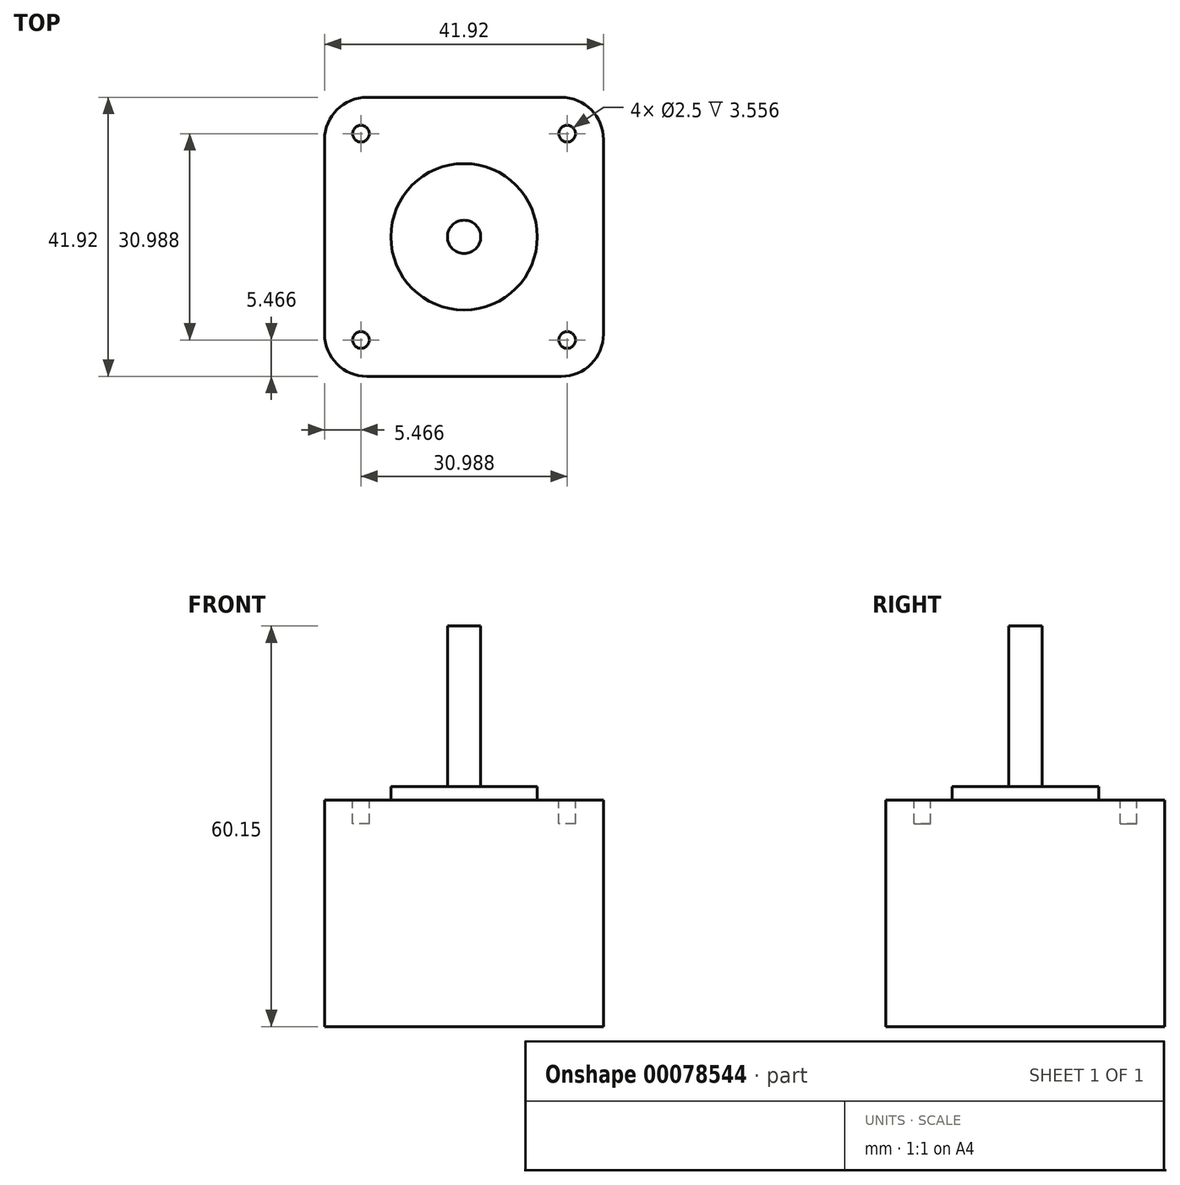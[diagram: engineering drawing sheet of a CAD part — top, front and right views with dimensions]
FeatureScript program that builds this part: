
annotation { "Feature Type Name" : "Feature", "Feature Type Description" : "" }
export const myFeature = defineFeature(function(context is Context, id is Id, definition is map)
    precondition{}
    {
        {
            var Q0;
            Q0=qCreatedBy(makeId("Top.planeOp"),FACE);
            var sketch = newSketch(context, id + "F0", { "sketchPlane" : qUnion([Q0])});
            skLineSegment(sketch, "E0.bottom", {"start": v(20.96, -20.95) * mm, "end": v(-20.95, -20.96) * mm});
            skLineSegment(sketch, "E0.top", {"start": v(20.95, 20.96) * mm, "end": v(-20.96, 20.96) * mm});
            skLineSegment(sketch, "E0.left", {"start": v(20.96, -20.95) * mm, "end": v(20.96, 20.96) * mm});
            skLineSegment(sketch, "E0.right", {"start": v(-20.95, -20.96) * mm, "end": v(-20.96, 20.96) * mm});
            skPoint(sketch, "E0.middle", {"position": v(0, 0) * mm});
            skSolve(sketch);
        }
        {
            var Q0;
            Q0 = qSketchRegion(id + "F0", true);
            extrude(context, id + "F1", {"entities" : qUnion([Q0]), "depth" : 34.04 * mm});
        }
        {
            var Q0;
            Q0=makeQuery(id+"F1.opExtrude","CAP_FACE",FACE,{"disambiguationData":[OSD([sQuery(id+"F0.wireOp",EDGE,"E0.bottom"),sQuery(id+"F0.wireOp",EDGE,"E0.top"),sQuery(id+"F0.wireOp",EDGE,"E0.left"),sQuery(id+"F0.wireOp",EDGE,"E0.right")])],"isStart":false});
            var sketch = newSketch(context, id + "F2", { "sketchPlane" : qUnion([Q0])});
            skCircle(sketch, "E1", {"center": v(15.5, -15.5) * mm, "radius": 1.25 * mm});
            skLineSegment(sketch, "E2", {"start": v(0, -22.8) * mm, "end": v(0, 29.63) * mm, "construction": true});
            skLineSegment(sketch, "E3", {"start": v(-23.36, 0) * mm, "end": v(28.4, 0) * mm, "construction": true});
            skCircle(sketch, "E4.MirrorC", {"center": v(15.5, 15.5) * mm, "radius": 1.25 * mm});
            skCircle(sketch, "E5.MirrorC", {"center": v(-15.5, 15.5) * mm, "radius": 1.25 * mm});
            skCircle(sketch, "E6.MirrorC", {"center": v(-15.5, -15.5) * mm, "radius": 1.25 * mm});
            skSolve(sketch);
        }
        {
            var Q0;
            Q0 = qSketchRegion(id + "F2", true);
            extrude(context, id + "F3", {"entities" : qUnion([Q0]), "operationType" : NewBodyOperationType.REMOVE, "oppositeDirection" : true, "depth" : 3.56 * mm});
        }
        {
            var Q0;
            Q0=makeQuery(id+"F1.opExtrude","SWEPT_EDGE",EDGE,{"disambiguationData":[OSD([sQuery(id+"F0.wireOp",EDGE,"E0.bottom"),sQuery(id+"F0.wireOp",EDGE,"E0.right")])]});
            var Q1;
            Q1=makeQuery(id+"F1.opExtrude","SWEPT_EDGE",EDGE,{"disambiguationData":[OSD([sQuery(id+"F0.wireOp",EDGE,"E0.bottom"),sQuery(id+"F0.wireOp",EDGE,"E0.left")])]});
            var Q2;
            Q2=makeQuery(id+"F1.opExtrude","SWEPT_EDGE",EDGE,{"disambiguationData":[OSD([sQuery(id+"F0.wireOp",EDGE,"E0.top"),sQuery(id+"F0.wireOp",EDGE,"E0.left")])]});
            var Q3;
            Q3=makeQuery(id+"F1.opExtrude","SWEPT_EDGE",EDGE,{"disambiguationData":[OSD([sQuery(id+"F0.wireOp",EDGE,"E0.top"),sQuery(id+"F0.wireOp",EDGE,"E0.right")])]});
            fillet(context, id + "F4", {"entities" : qUnion([Q0, Q1, Q2, Q3]), "radius" : 6.35 * mm, "tangentPropagation" : true, "allowEdgeOverflow" : false});
        }
        {
            var Q0;
            Q0=makeQuery(id+"F1.opExtrude","CAP_FACE",FACE,{"disambiguationData":[OSD([sQuery(id+"F0.wireOp",EDGE,"E0.bottom"),sQuery(id+"F0.wireOp",EDGE,"E0.top"),sQuery(id+"F0.wireOp",EDGE,"E0.left"),sQuery(id+"F0.wireOp",EDGE,"E0.right")])],"isStart":false});
            var sketch = newSketch(context, id + "F5", { "sketchPlane" : qUnion([Q0])});
            skCircle(sketch, "E7", {"center": v(0, 0) * mm, "radius": 11 * mm});
            skSolve(sketch);
        }
        {
            var Q0;
            Q0 = qSketchRegion(id + "F5", true);
            extrude(context, id + "F6", {"entities" : qUnion([Q0]), "operationType" : NewBodyOperationType.ADD, "depth" : 1.98 * mm});
        }
        {
            var Q0;
            Q0=makeQuery(id+"F6.opExtrude","CAP_FACE",FACE,{"disambiguationData":[OSD([sQuery(id+"F5.wireOp",EDGE,"E7")])],"isStart":false});
            var sketch = newSketch(context, id + "F7", { "sketchPlane" : qUnion([Q0])});
            skCircle(sketch, "E8", {"center": v(0, 0) * mm, "radius": 2.5 * mm});
            skSolve(sketch);
        }
        {
            var Q0;
            Q0 = qSketchRegion(id + "F7", true);
            extrude(context, id + "F8", {"entities" : qUnion([Q0]), "operationType" : NewBodyOperationType.ADD, "depth" : 24.13 * mm});
        }
    });
